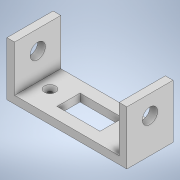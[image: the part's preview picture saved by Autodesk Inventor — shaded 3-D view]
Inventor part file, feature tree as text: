
AUTODESK INVENTOR PART (.ipt)
format: ipt  version: 2022 (Build 260153000, 153)  size: 147,456 bytes
history: native  units: mm
features: extrude x5, sketch x5
ambient origin geometry x8: Origin, YZ Plane, XZ Plane, XY Plane, X Axis, Y Axis, Z Axis, Center Point
bodies: Solid1 (feature_tree)
feature tree (10):
  extrude  "Extrusion1"  Depth=5.0mm
  extrude  "Extrusion2"  Depth=68.0mm
  extrude  "Extrusion3"  Depth=30.0mm TaperAngle=0.0deg
  extrude  "Extrusion4"  Depth=15.0mm
  extrude  "Extrusion5"  Depth=15.0mm TaperAngle=0.0deg
  sketch  "Sketch1"  dims[d0=35.0mm d1=5.0mm]
  sketch  "Sketch2"  dims[d2=30.0mm d3=68.0mm]
  sketch  "Sketch3"  dims[d4=5.0mm d5=30.0mm d6=0.0mm]
  sketch  "Sketch4"  dims[d7=10.0mm d8=15.0mm]
  sketch  "Sketch5"  dims[d9=12.5mm d10=1000.0mm d11=0.0mm d12=7.25mm d13=15.0mm d14=8.0mm d15=7.25mm d16=8.0mm d17=15.0mm d18=2.1735mm d19=-7.853982mm d20=10.0mm d21=0.0mm d22=28.0mm d23=15.0mm d24=15.0mm d25=34.0mm d26=0.0mm d27=0.0mm]
